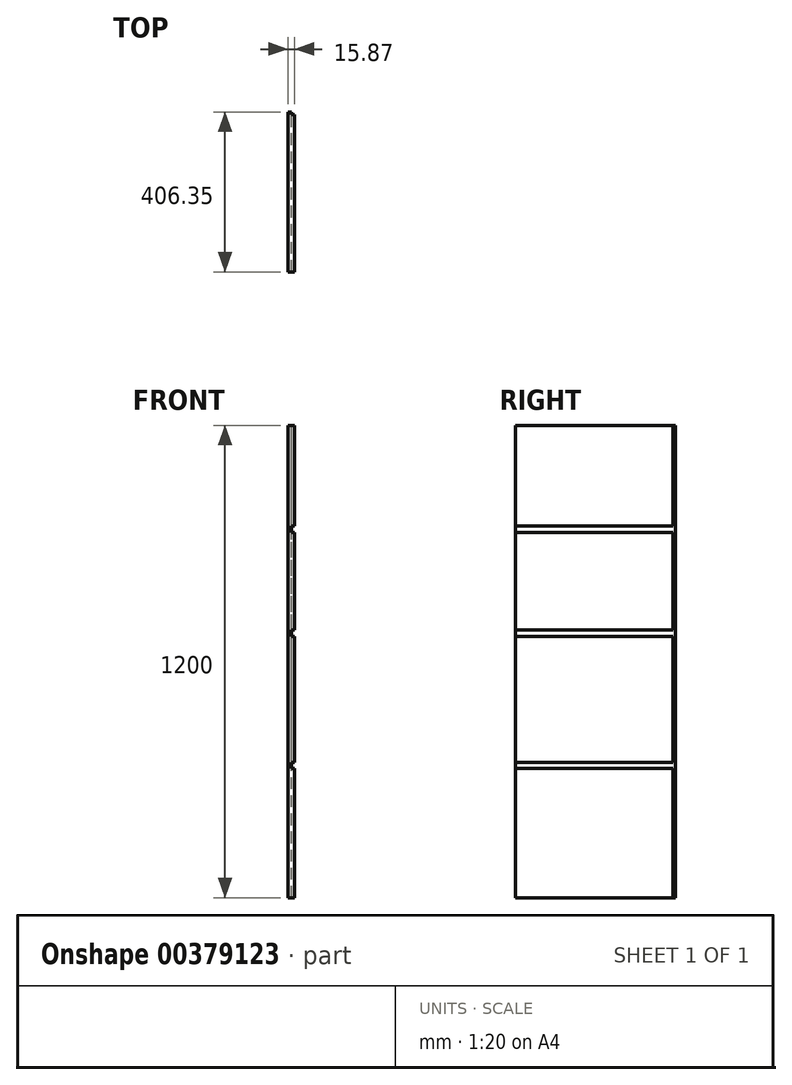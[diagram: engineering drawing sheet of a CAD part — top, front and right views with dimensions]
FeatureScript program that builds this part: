
annotation { "Feature Type Name" : "Feature", "Feature Type Description" : "" }
export const myFeature = defineFeature(function(context is Context, id is Id, definition is map)
    precondition{}
    {
        {
            var Q0;
            Q0=qCreatedBy(makeId("Front.planeOp"),FACE);
            var sketch = newSketch(context, id + "F0", { "sketchPlane" : qUnion([Q0])});
            skLineSegment(sketch, "E0.bottom", {"start": v(-45.4, 967.8) * mm, "end": v(-29.52, 967.8) * mm});
            skLineSegment(sketch, "E0.top", {"start": v(-45.4, -232.2) * mm, "end": v(-29.52, -232.2) * mm});
            skLineSegment(sketch, "E0.left", {"start": v(-45.4, 967.8) * mm, "end": v(-45.4, -232.2) * mm});
            skLineSegment(sketch, "E0.right", {"start": v(-29.52, 967.8) * mm, "end": v(-29.52, -232.2) * mm});
            skLineSegment(sketch, "E1.bottom", {"start": v(-29.52, 111.6) * mm, "end": v(-37.46, 111.6) * mm});
            skLineSegment(sketch, "E1.top", {"start": v(-29.52, 95.73) * mm, "end": v(-37.46, 95.73) * mm});
            skLineSegment(sketch, "E1.left", {"start": v(-29.52, 111.6) * mm, "end": v(-29.52, 95.73) * mm});
            skLineSegment(sketch, "E1.right", {"start": v(-37.46, 111.6) * mm, "end": v(-37.46, 95.73) * mm});
            skLineSegment(sketch, "E2.bottom", {"start": v(-29.52, 431.6) * mm, "end": v(-37.46, 431.6) * mm});
            skLineSegment(sketch, "E2.top", {"start": v(-29.52, 447.48) * mm, "end": v(-37.46, 447.48) * mm});
            skLineSegment(sketch, "E2.left", {"start": v(-29.52, 431.6) * mm, "end": v(-29.52, 447.48) * mm});
            skLineSegment(sketch, "E2.right", {"start": v(-37.46, 431.6) * mm, "end": v(-37.46, 447.48) * mm});
            skLineSegment(sketch, "E3.bottom", {"start": v(-29.52, 695.73) * mm, "end": v(-37.46, 695.73) * mm});
            skLineSegment(sketch, "E3.top", {"start": v(-29.52, 711.6) * mm, "end": v(-37.46, 711.6) * mm});
            skLineSegment(sketch, "E3.left", {"start": v(-29.52, 695.73) * mm, "end": v(-29.52, 711.6) * mm});
            skLineSegment(sketch, "E3.right", {"start": v(-37.46, 695.73) * mm, "end": v(-37.46, 711.6) * mm});
            skSolve(sketch);
        }
        {
            var Q0;
            {var subQ10=sQuery(id+"F0.wireOp",EDGE,"E0.bottom");Q0=makeQuery(id+"F0.imprint","IMPRINT",FACE,{"disambiguationData":[TD([[makeQuery(id+"F0.imprint","IMPRINT",EDGE,{"derivedFrom":subQ10}),-1.0]])]});}
            extrude(context, id + "F1", {"entities" : qUnion([Q0]), "depth" : 406.35 * mm});
        }
        {
            var Q0;
            Q0=makeQuery(id+"F1.opExtrude","SWEPT_FACE",FACE,{"disambiguationData":[OSD([sQuery(id+"F0.wireOp",EDGE,"E0.bottom")])]});
            var sketch = newSketch(context, id + "F2", { "sketchPlane" : qUnion([Q0])});
            skLineSegment(sketch, "E4.bottom", {"start": v(-29.52, 0) * mm, "end": v(-37.46, 0) * mm});
            skLineSegment(sketch, "E4.top", {"start": v(-29.52, -6.35) * mm, "end": v(-37.46, -6.35) * mm});
            skLineSegment(sketch, "E4.left", {"start": v(-29.52, 0) * mm, "end": v(-29.52, -6.35) * mm});
            skLineSegment(sketch, "E4.right", {"start": v(-37.46, 0) * mm, "end": v(-37.46, -6.35) * mm});
            skSolve(sketch);
        }
        {
            var Q0;
            Q0=makeQuery(id+"F2.imprint","IMPRINT",FACE,{"disambiguationData":[TD([[makeQuery(id+"F2.imprint","IMPRINT",EDGE,{"derivedFrom":sQuery(id+"F2.wireOp",EDGE,"E4.bottom")}),-1.0]])]});
            extrude(context, id + "F3", {"entities" : qUnion([Q0]), "operationType" : NewBodyOperationType.REMOVE, "endBound" : BoundingType.THROUGH_ALL, "oppositeDirection" : true, "depth" : 25 * mm});
        }
    });
